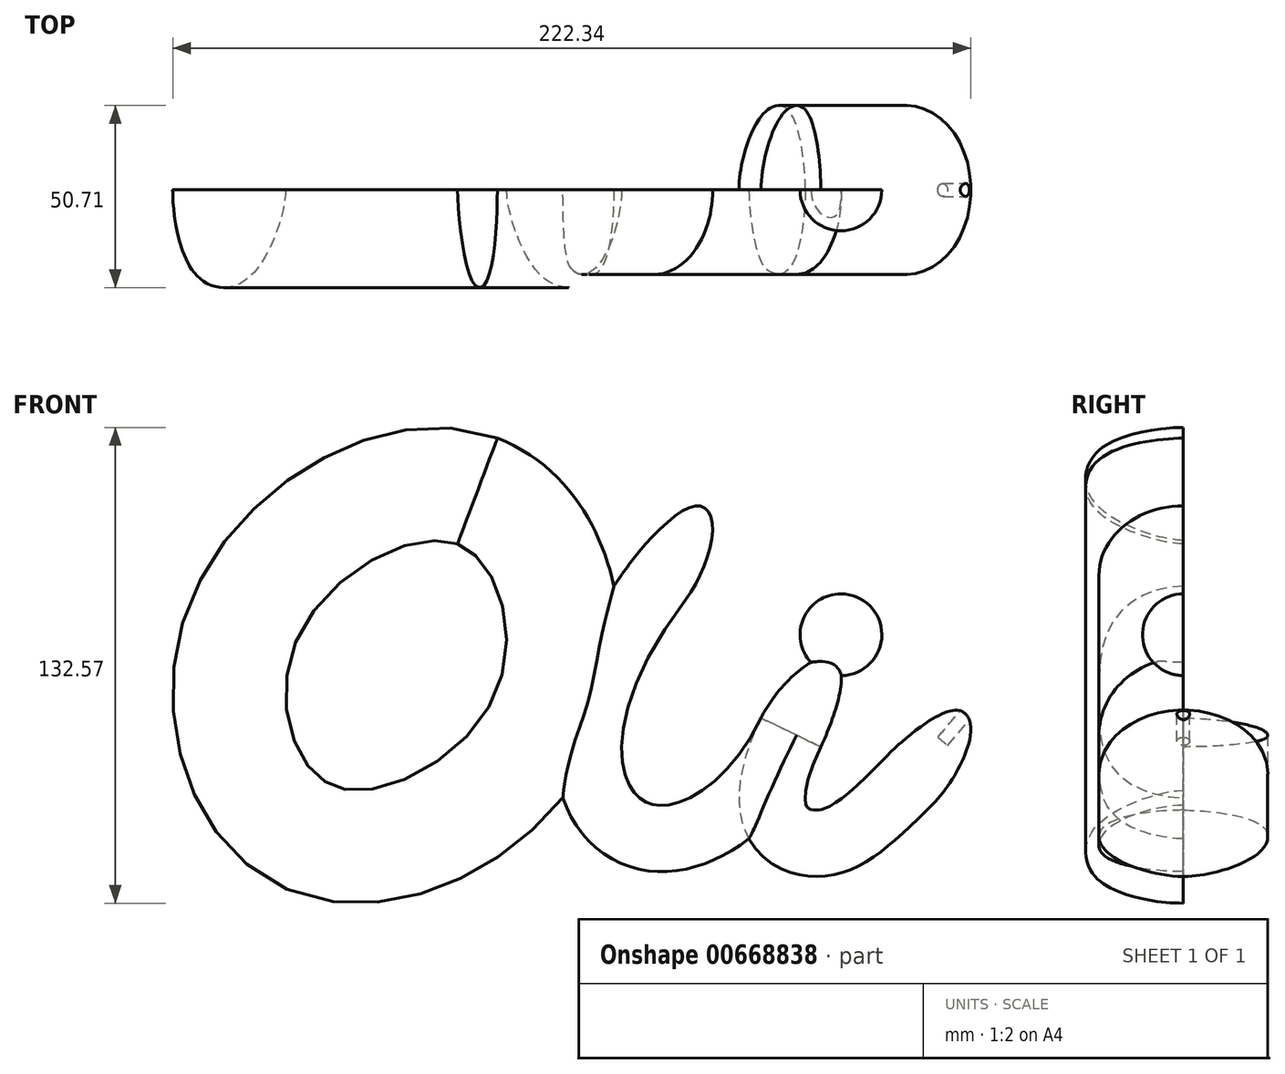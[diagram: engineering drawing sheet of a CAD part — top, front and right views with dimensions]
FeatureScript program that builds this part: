
annotation { "Feature Type Name" : "Feature", "Feature Type Description" : "" }
export const myFeature = defineFeature(function(context is Context, id is Id, definition is map)
    precondition{}
    {
        {
            var Q0;
            Q0=qCreatedBy(makeId("Front.planeOp"),FACE);
            var sketch = newSketch(context, id + "F0", { "sketchPlane" : qUnion([Q0])});
            skFitSpline(sketch, "E0", {"points": [v(-92.52, 38.27) * mm, v(-98.74, -32.75) * mm, v(-55.9, -4.39) * mm], "startDerivative": vector(-161.46, -212.9) * mm, "endDerivative": vector(72.76, 150.27) * mm});
            skFitSpline(sketch, "E1", {"points": [v(-55.9, -4.39) * mm, v(-50.29, -35.2) * mm, v(-22.36, -17.24) * mm], "startDerivative": vector(-67.81, -140.04) * mm, "endDerivative": vector(76.1, 78.04) * mm});
            skFitSpline(sketch, "E2", {"points": [v(-145.26, 57.42) * mm, v(-202.93, 24.73) * mm, v(-186.63, -28.72) * mm, v(-128.98, 2.73) * mm, v(-145.26, 57.42) * mm]});
            skCircle(sketch, "E3", {"center": v(-41.95, 22.84) * mm, "radius": 11.38 * mm});
            skLineSegment(sketch, "E4", {"start": v(-41.95, 34.22) * mm, "end": v(-41.95, 11.45) * mm});
            skSolve(sketch);
        }
        {
            var Q0;
            Q0=sQuery(id+"F0.wireOp",VERTEX,"E2.0.internal");
            var Q1;
            Q1=sQuery(id+"F0.wireOp",EDGE,"E2");
            cPlane(context, id + "F1", {"entities" : qUnion([Q0, Q1]), "cplaneType" : CPlaneType.CURVE_POINT, "offset" : 25 * mm, "width" : 150 * mm, "height" : 150 * mm});
        }
        {
            var Q0;
            Q0=sQuery(id+"F0.wireOp",VERTEX,"E1.0.internal");
            var Q1;
            Q1=sQuery(id+"F0.wireOp",EDGE,"E1");
            cPlane(context, id + "F2", {"entities" : qUnion([Q0, Q1]), "cplaneType" : CPlaneType.CURVE_POINT, "offset" : 25 * mm, "width" : 150 * mm, "height" : 150 * mm});
        }
        {
            var Q0;
            Q0=qCreatedBy(id+"F1.planeOp",FACE);
            var sketch = newSketch(context, id + "F3", { "sketchPlane" : qUnion([Q0])});
            skPoint(sketch, "E5.0", {"position": v(0, 2.65) * mm});
            skFitSpline(sketch, "E6", {"points": [v(0, 24.21) * mm, v(23.73, 17.65) * mm, v(24.5, 3.1) * mm, v(0, -7.26) * mm], "startDerivative": vector(55.73, 0) * mm, "endDerivative": vector(-44.82, 0) * mm});
            skLineSegment(sketch, "E7", {"start": v(0, -7.26) * mm, "end": v(0, 24.21) * mm});
            skSolve(sketch);
        }
        {
            var Q0;
            Q0=qCreatedBy(id+"F2.planeOp",FACE);
            var sketch = newSketch(context, id + "F4", { "sketchPlane" : qUnion([Q0])});
            skLineSegment(sketch, "E8", {"start": v(-39.15, 0) * mm, "end": v(-57.63, 0) * mm});
            skFitSpline(sketch, "E9", {"points": [v(-57.63, 0) * mm, v(-50.72, 21.38) * mm, v(-44.08, 22.43) * mm, v(-39.15, 0) * mm], "startDerivative": vector(0, 54.16) * mm, "endDerivative": vector(0, -57.45) * mm});
            skSolve(sketch);
        }
        {
            var Q0;
            Q0=makeQuery(id+"F3.imprint","IMPRINT",FACE,{"disambiguationData":[TD([[makeQuery(id+"F3.imprint","IMPRINT",EDGE,{"derivedFrom":sQuery(id+"F3.wireOp",EDGE,"E6")}),-1.0]])]});
            var Q1;
            Q1=sQuery(id+"F0.wireOp",EDGE,"E2");
            sweep(context, id + "F5", {"profiles" : qUnion([Q0]), "path" : qUnion([Q1])});
        }
        {
            var Q0;
            Q0=makeQuery(id+"F4.imprint","IMPRINT",FACE,{"disambiguationData":[TD([[makeQuery(id+"F4.imprint","IMPRINT",EDGE,{"derivedFrom":sQuery(id+"F4.wireOp",EDGE,"E8")}),-1.0]])]});
            var Q1;
            Q1=sQuery(id+"F0.wireOp",EDGE,"E0");
            sweep(context, id + "F6", {"operationType" : NewBodyOperationType.ADD, "profiles" : qUnion([Q0]), "path" : qUnion([Q1])});
        }
        {
            var Q0;
            Q0=makeQuery(id+"F4.imprint","IMPRINT",FACE,{"disambiguationData":[TD([[makeQuery(id+"F4.imprint","IMPRINT",EDGE,{"derivedFrom":sQuery(id+"F4.wireOp",EDGE,"E8")}),-1.0]])]});
            var Q1;
            Q1=sQuery(id+"F0.wireOp",EDGE,"E1");
            sweep(context, id + "F7", {"profiles" : qUnion([Q0]), "path" : qUnion([Q1])});
        }
        {
            var Q0;
            Q0=makeQuery(id+"F7.opSweep","CAP_FACE",FACE,{"disambiguationData":[OSD([sQuery(id+"F0.wireOp",VERTEX,"E1.end"),sQuery(id+"F4.wireOp",EDGE,"E8"),sQuery(id+"F4.wireOp",EDGE,"E9")])],"isStart":false});
            var Q1;
            Q1=makeQuery(id+"F7.opSweep","CAP_EDGE",EDGE,{"disambiguationData":[OSD([sQuery(id+"F0.wireOp",VERTEX,"E1.end"),sQuery(id+"F4.wireOp",EDGE,"E8")])],"isStart":false});
            revolve(context, id + "F8", {"operationType" : NewBodyOperationType.ADD, "entities" : qUnion([Q0]), "axis" : qUnion([Q1]), "revolveType" : RevolveType.ONE_DIRECTION, "oppositeDirection" : true, "angle" : 90 * degree});
        }
        {
            var Q0;
            Q0=makeQuery(id+"F4.imprint","IMPRINT",FACE,{"disambiguationData":[TD([[makeQuery(id+"F4.imprint","IMPRINT",EDGE,{"derivedFrom":sQuery(id+"F4.wireOp",EDGE,"E8")}),-1.0]])]});
            var Q1;
            Q1=sQuery(id+"F4.wireOp",EDGE,"E8");
            revolve(context, id + "F9", {"entities" : qUnion([Q0]), "axis" : qUnion([Q1]), "revolveType" : RevolveType.ONE_DIRECTION, "angle" : 90 * degree});
        }
        {
            var Q0;
            Q0=makeQuery(id+"F6.opSweep","CAP_FACE",FACE,{"disambiguationData":[OSD([sQuery(id+"F0.wireOp",VERTEX,"E0.start"),sQuery(id+"F4.wireOp",EDGE,"E8"),sQuery(id+"F4.wireOp",EDGE,"E9")])],"isStart":false});
            var Q1;
            Q1=makeQuery(id+"F6.opSweep","CAP_EDGE",EDGE,{"disambiguationData":[OSD([sQuery(id+"F0.wireOp",VERTEX,"E0.start"),sQuery(id+"F4.wireOp",EDGE,"E8")])],"isStart":false});
            revolve(context, id + "F10", {"operationType" : NewBodyOperationType.ADD, "entities" : qUnion([Q0]), "axis" : qUnion([Q1]), "revolveType" : RevolveType.ONE_DIRECTION, "oppositeDirection" : true, "angle" : 90 * degree});
        }
        {
            var Q0;
            {var subQ0=sQuery(id+"F0.wireOp",EDGE,"E4");Q0=makeQuery(id+"F0.imprint","IMPRINT",FACE,{"disambiguationData":[TD([[makeQuery(id+"F0.imprint","IMPRINT",EDGE,{"derivedFrom":subQ0}),-1.0]])]});}
            var Q1;
            Q1=sQuery(id+"F0.wireOp",EDGE,"E4");
            revolve(context, id + "F11", {"operationType" : NewBodyOperationType.ADD, "entities" : qUnion([Q0]), "axis" : qUnion([Q1]), "revolveType" : RevolveType.ONE_DIRECTION, "oppositeDirection" : true, "angle" : 180 * degree});
        }
        {
            var Q0;
            {var subQ0=sQuery(id+"F4.wireOp",EDGE,"E8");Q0=makeQuery(id+"F8.boolean.opBoolean","MERGE",FACE,{"derivedFrom":[makeQuery(id+"F7.opSweep","SWEPT_FACE",FACE,{"disambiguationData":[OSD([sQuery(id+"F0.wireOp",EDGE,"E1"),subQ0])]}),makeQuery(id+"F8.opRevolve","CAP_FACE",FACE,{"disambiguationData":[OSD([sQuery(id+"F0.wireOp",VERTEX,"E1.end"),subQ0,sQuery(id+"F4.wireOp",EDGE,"E9")])],"isStart":false})]});}
            var sketch = newSketch(context, id + "F12", { "sketchPlane" : qUnion([Q0])});
            skLineSegment(sketch, "E10", {"start": v(7.16, 0.78) * mm, "end": v(12.64, -5.76) * mm});
            skSolve(sketch);
        }
        {
            var Q0;
            Q0=sQuery(id+"F12.wireOp",EDGE,"E10");
            var Q1;
            Q1=sQuery(id+"F12.wireOp",VERTEX,"E10.start");
            cPlane(context, id + "F13", {"entities" : qUnion([Q0, Q1]), "cplaneType" : CPlaneType.LINE_POINT, "offset" : 25 * mm, "width" : 150 * mm, "height" : 150 * mm});
        }
        {
            var Q0;
            Q0=qCreatedBy(id+"F13.planeOp",FACE);
            var sketch = newSketch(context, id + "F14", { "sketchPlane" : qUnion([Q0])});
            skCircle(sketch, "E11", {"center": v(-5.99, 0) * mm, "radius": 1.79 * mm});
            skSolve(sketch);
        }
        {
            var Q0;
            Q0=makeQuery(id+"F14.imprint","IMPRINT",FACE,{"disambiguationData":[TD([[makeQuery(id+"F14.imprint","IMPRINT",EDGE,{"derivedFrom":sQuery(id+"F14.wireOp",EDGE,"E11")}),1.0]])]});
            extrude(context, id + "F15", {"entities" : qUnion([Q0]), "operationType" : NewBodyOperationType.REMOVE, "endBound" : BoundingType.SYMMETRIC, "depth" : 20 * mm, "offsetDistance" : 25 * mm});
        }
        {
            var Q0;
            Q0=makeQuery(id+"F7.opSweep","SWEPT_BODY",BODY,{"disambiguationData":[OSD([sQuery(id+"F0.wireOp",EDGE,"E1"),sQuery(id+"F4.wireOp",EDGE,"E8"),sQuery(id+"F4.wireOp",EDGE,"E9")])]});
            var Q1;
            Q1=qCreatedBy(makeId("Front.planeOp"),FACE);
            mirror(context, id + "F16", {"operationType" : NewBodyOperationType.ADD, "entities" : qUnion([Q0]), "mirrorPlane" : qUnion([Q1])});
        }
    });
